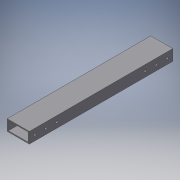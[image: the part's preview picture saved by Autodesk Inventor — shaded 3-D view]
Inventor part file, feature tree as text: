
AUTODESK INVENTOR PART (.ipt)
format: ipt  version: 2018 (Build 220112000, 112)  size: 145,920 bytes
history: native  units: in
note: dims shown in document units (in); Inventor stores cm internally (conversion verified against a paired STEP export)
features: extrude x3, sketch x3
ambient origin geometry x8: Origin, YZ Plane, XZ Plane, XY Plane, X Axis, Y Axis, Z Axis, Center Point
bodies: Solid1 (feature_tree)
feature tree (6):
  extrude  "Extrusion1"  Depth=2.0in
  extrude  "Extrusion2"  Depth=0.1in
  extrude  "Extrusion3"  Depth=0.1in
  sketch  "Sketch1"  dims[d0=1.0in d1=2.0in]
  sketch  "Sketch2"  dims[d2=0.1in d3=0.1in]
  sketch  "Sketch3"  dims[d4=0.1in d5=0.1in d6=13.0in d7=0.0in d8=0.5in d9=1.0in d10=1.0in d11=1.0in d12=1.0in d13=0.5in d14=0.2031in d15=0.2031in d16=0.2031in d19=0.2031in d20=0.2031in d21=0.2031in d22=0.5in d23=0.5in d24=0.5in d25=0.5in d26=0.5in d27=0.5in d28=11.0in d29=0.0in d30=0.2031in d31=0.2031in d32=0.5in d33=1.0in d34=11.0in d35=0.0in]
